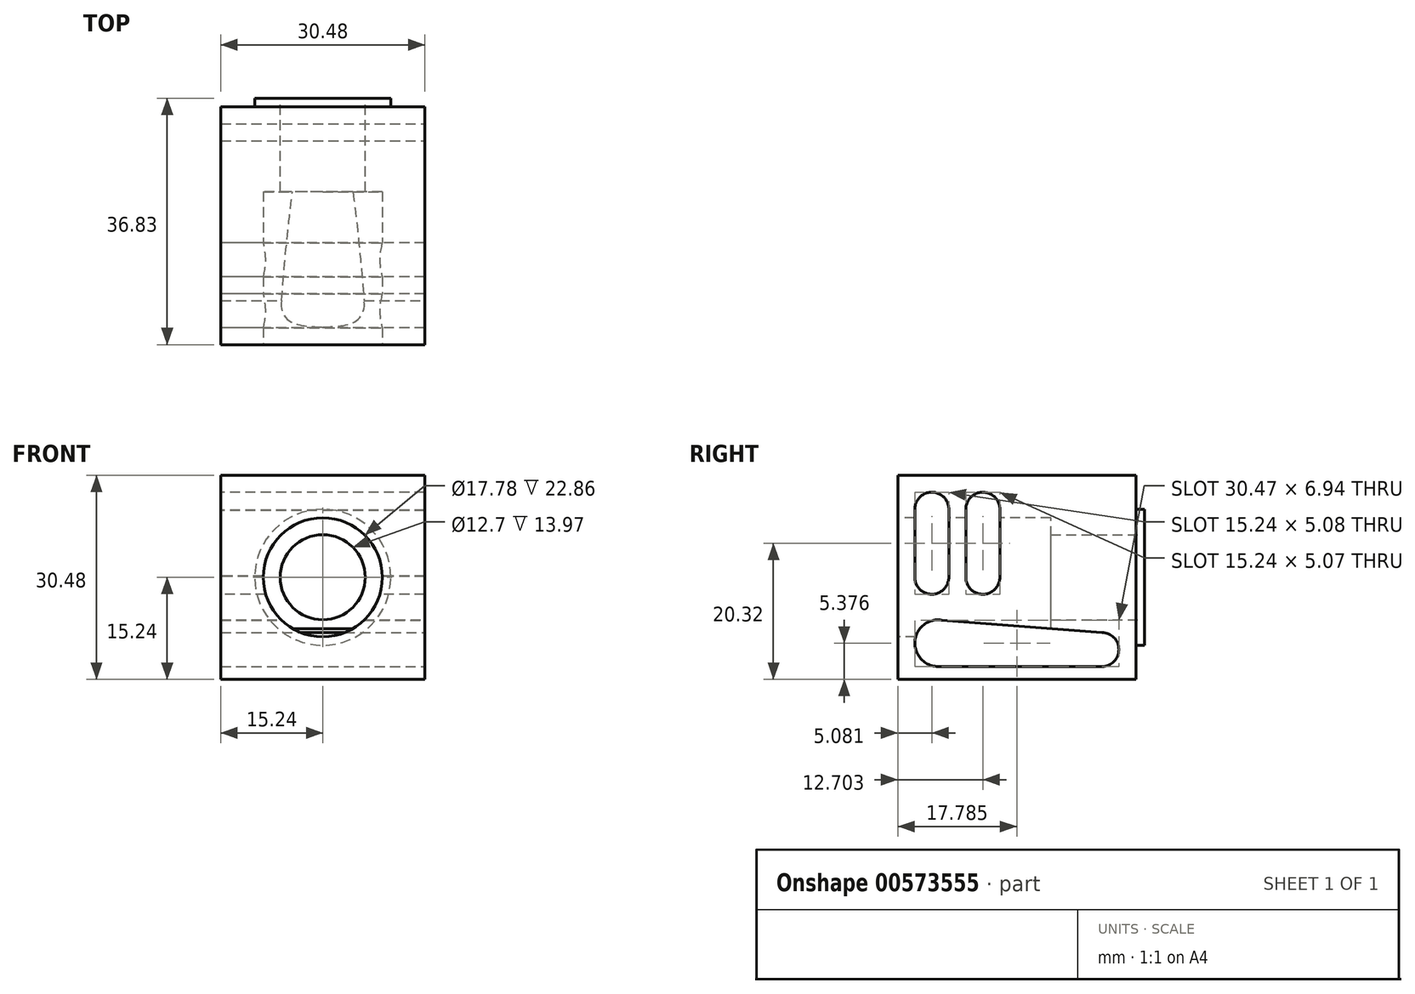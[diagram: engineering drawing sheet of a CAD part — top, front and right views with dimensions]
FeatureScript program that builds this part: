
annotation { "Feature Type Name" : "Feature", "Feature Type Description" : "" }
export const myFeature = defineFeature(function(context is Context, id is Id, definition is map)
    precondition{}
    {
        {
            var Q0;
            Q0=qCreatedBy(makeId("Front.planeOp"),FACE);
            var sketch = newSketch(context, id + "F0", { "sketchPlane" : qUnion([Q0])});
            skLineSegment(sketch, "E0.bottom", {"start": v(-15.24, -15.24) * mm, "end": v(15.24, -15.24) * mm});
            skLineSegment(sketch, "E0.top", {"start": v(-15.24, 15.24) * mm, "end": v(15.24, 15.24) * mm});
            skLineSegment(sketch, "E0.left", {"start": v(-15.24, -15.24) * mm, "end": v(-15.24, 15.24) * mm});
            skLineSegment(sketch, "E0.right", {"start": v(15.24, -15.24) * mm, "end": v(15.24, 15.24) * mm});
            skPoint(sketch, "E0.middle", {"position": v(0, 0) * mm});
            skSolve(sketch);
        }
        {
            var Q0;
            Q0 = qSketchRegion(id + "F0", true);
            extrude(context, id + "F1", {"entities" : qUnion([Q0]), "depth" : 35.56 * mm, "offsetDistance" : 25.4 * mm});
        }
        {
            var Q0;
            Q0=makeQuery(id+"F1.opExtrude","SWEPT_FACE",FACE,{"disambiguationData":[OSD([sQuery(id+"F0.wireOp",EDGE,"E0.left")])]});
            var sketch = newSketch(context, id + "F2", { "sketchPlane" : qUnion([Q0])});
            skCircle(sketch, "E1", {"center": v(30.48, 10.16) * mm, "radius": 2.54 * mm});
            skCircle(sketch, "E2", {"center": v(30.48, 0) * mm, "radius": 2.54 * mm});
            skCircle(sketch, "E3", {"center": v(22.86, 10.16) * mm, "radius": 2.54 * mm});
            skCircle(sketch, "E4", {"center": v(22.86, 0) * mm, "radius": 2.54 * mm});
            skLineSegment(sketch, "E5", {"start": v(20.32, 10.3) * mm, "end": v(20.32, -0.13) * mm});
            skLineSegment(sketch, "E6", {"start": v(20.32, -0.13) * mm, "end": v(20.32, 10.3) * mm});
            skLineSegment(sketch, "E7", {"start": v(25.4, 9.95) * mm, "end": v(25.4, -0.2) * mm});
            skLineSegment(sketch, "E8", {"start": v(27.94, 10.16) * mm, "end": v(27.94, 0) * mm});
            skLineSegment(sketch, "E9", {"start": v(33.02, 10.05) * mm, "end": v(33.02, -0.1) * mm});
            skSolve(sketch);
        }
        {
            var Q0;
            Q0 = qSketchRegion(id + "F2", true);
            extrude(context, id + "F3", {"entities" : qUnion([Q0]), "operationType" : NewBodyOperationType.REMOVE, "oppositeDirection" : true, "depth" : 38.1 * mm, "offsetDistance" : 25.4 * mm});
        }
        {
            var Q0;
            Q0=makeQuery(id+"F1.opExtrude","SWEPT_FACE",FACE,{"disambiguationData":[OSD([sQuery(id+"F0.wireOp",EDGE,"E0.right")])]});
            var sketch = newSketch(context, id + "F4", { "sketchPlane" : qUnion([Q0])});
            skCircle(sketch, "E10", {"center": v(-29.53, -9.84) * mm, "radius": 3.5 * mm});
            skCircle(sketch, "E11", {"center": v(-5.08, -10.8) * mm, "radius": 2.54 * mm});
            skLineSegment(sketch, "E12", {"start": v(-29.53, -13.34) * mm, "end": v(-5.08, -13.34) * mm});
            skLineSegment(sketch, "E13", {"start": v(-29.53, -6.35) * mm, "end": v(-5.08, -8.26) * mm});
            skSolve(sketch);
        }
        {
            var Q0;
            Q0 = qSketchRegion(id + "F4", true);
            extrude(context, id + "F5", {"entities" : qUnion([Q0]), "operationType" : NewBodyOperationType.REMOVE, "oppositeDirection" : true, "depth" : 38.1 * mm, "offsetDistance" : 25.4 * mm});
        }
        {
            var Q0;
            Q0=makeQuery(id+"F1.opExtrude","CAP_FACE",FACE,{"disambiguationData":[OSD([sQuery(id+"F0.wireOp",EDGE,"E0.bottom"),sQuery(id+"F0.wireOp",EDGE,"E0.top"),sQuery(id+"F0.wireOp",EDGE,"E0.left"),sQuery(id+"F0.wireOp",EDGE,"E0.right")])],"isStart":false});
            var sketch = newSketch(context, id + "F6", { "sketchPlane" : qUnion([Q0])});
            skCircle(sketch, "E14", {"center": v(0, 0) * mm, "radius": 8.89 * mm});
            skSolve(sketch);
        }
        {
            var Q0;
            Q0 = qSketchRegion(id + "F6", true);
            extrude(context, id + "F7", {"entities" : qUnion([Q0]), "operationType" : NewBodyOperationType.REMOVE, "oppositeDirection" : true, "depth" : 22.86 * mm, "offsetDistance" : 25.4 * mm});
        }
        {
            var Q0;
            Q0=makeQuery(id+"F1.opExtrude","CAP_FACE",FACE,{"disambiguationData":[OSD([sQuery(id+"F0.wireOp",EDGE,"E0.bottom"),sQuery(id+"F0.wireOp",EDGE,"E0.top"),sQuery(id+"F0.wireOp",EDGE,"E0.left"),sQuery(id+"F0.wireOp",EDGE,"E0.right")])],"isStart":true});
            var sketch = newSketch(context, id + "F8", { "sketchPlane" : qUnion([Q0])});
            skCircle(sketch, "E15", {"center": v(0, 0) * mm, "radius": 10.16 * mm});
            skSolve(sketch);
        }
        {
            var Q0;
            Q0 = qSketchRegion(id + "F8", true);
            extrude(context, id + "F9", {"entities" : qUnion([Q0]), "operationType" : NewBodyOperationType.ADD, "depth" : 1.27 * mm, "offsetDistance" : 25.4 * mm});
        }
        {
            var Q0;
            Q0=makeQuery(id+"F1.opExtrude","CAP_FACE",FACE,{"disambiguationData":[OSD([sQuery(id+"F0.wireOp",EDGE,"E0.bottom"),sQuery(id+"F0.wireOp",EDGE,"E0.top"),sQuery(id+"F0.wireOp",EDGE,"E0.left"),sQuery(id+"F0.wireOp",EDGE,"E0.right")])],"isStart":true});
            var sketch = newSketch(context, id + "F10", { "sketchPlane" : qUnion([Q0])});
            skCircle(sketch, "E16", {"center": v(0, 0) * mm, "radius": 6.35 * mm});
            skSolve(sketch);
        }
        {
            var Q0;
            Q0 = qSketchRegion(id + "F10", true);
            extrude(context, id + "F11", {"entities" : qUnion([Q0]), "operationType" : NewBodyOperationType.REMOVE, "oppositeDirection" : true, "depth" : 38.1 * mm, "offsetDistance" : 25.4 * mm});
        }
        {
            var Q0;
            Q0=makeQuery(id+"F11.boolean.opBoolean","COPY",FACE,{"derivedFrom":makeQuery(id+"F11.opExtrude","CAP_FACE",FACE,{"disambiguationData":[OSD([sQuery(id+"F10.wireOp",EDGE,"E16")])],"isStart":true})});
            var sketch = newSketch(context, id + "F12", { "sketchPlane" : qUnion([Q0])});
            skCircle(sketch, "E17", {"center": v(0, 0) * mm, "radius": 6.35 * mm});
            skSolve(sketch);
        }
        {
            var Q0;
            Q0 = qSketchRegion(id + "F12", true);
            extrude(context, id + "F13", {"entities" : qUnion([Q0]), "operationType" : NewBodyOperationType.REMOVE, "oppositeDirection" : true, "depth" : 25.4 * mm, "offsetDistance" : 25.4 * mm});
        }
    });
